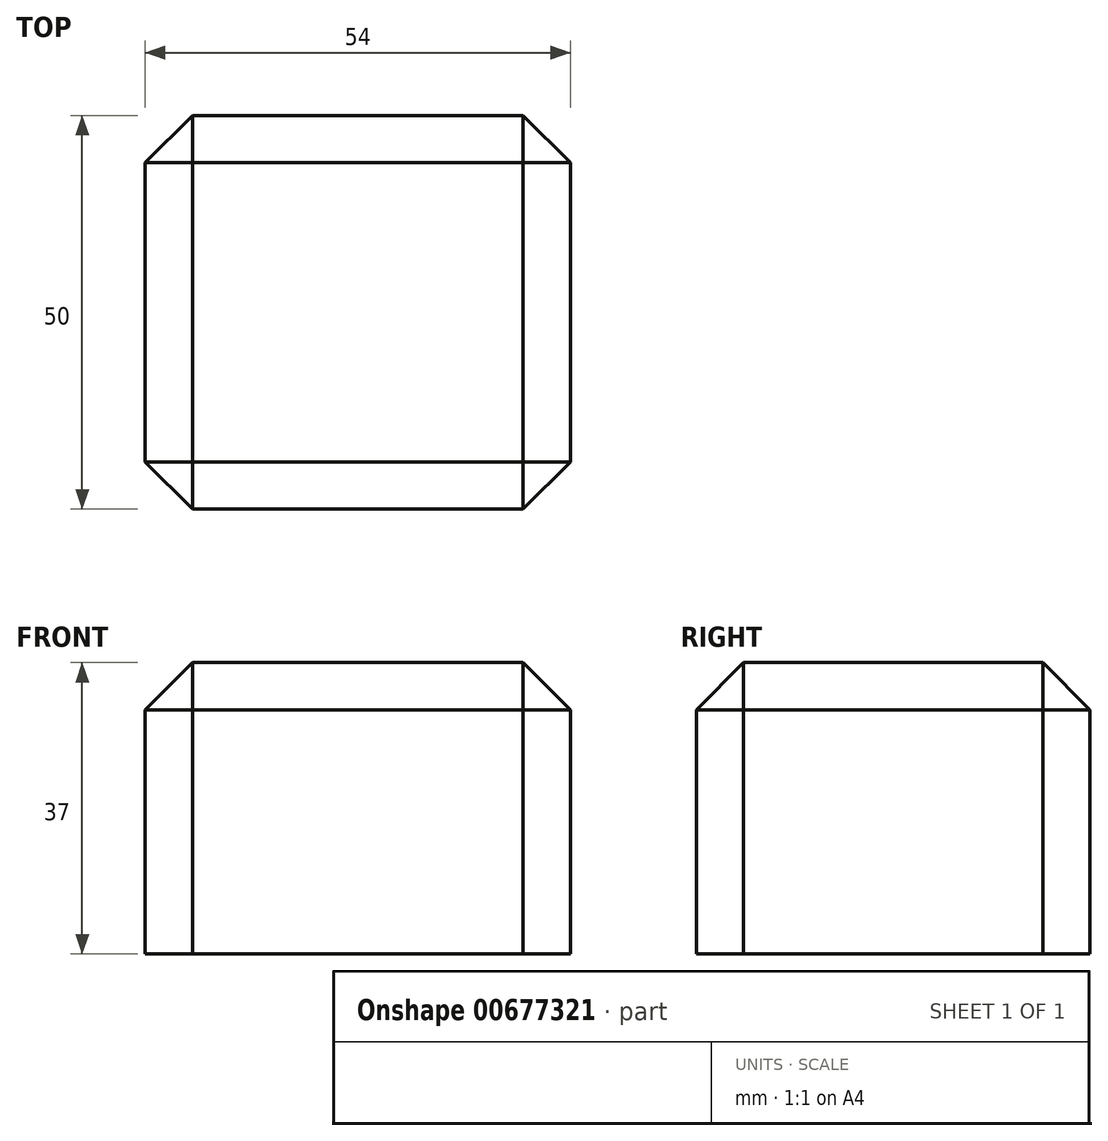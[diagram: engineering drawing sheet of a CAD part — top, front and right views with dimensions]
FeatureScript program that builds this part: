
annotation { "Feature Type Name" : "Feature", "Feature Type Description" : "" }
export const myFeature = defineFeature(function(context is Context, id is Id, definition is map)
    precondition{}
    {
        {
            var Q0;
            Q0=qCreatedBy(makeId("Top.planeOp"),FACE);
            var sketch = newSketch(context, id + "F0", { "sketchPlane" : qUnion([Q0])});
            skLineSegment(sketch, "E0.bottom", {"start": v(27, 25) * mm, "end": v(-27, 25) * mm});
            skLineSegment(sketch, "E0.top", {"start": v(27, -25) * mm, "end": v(-27, -25) * mm});
            skLineSegment(sketch, "E0.left", {"start": v(27, 25) * mm, "end": v(27, -25) * mm});
            skLineSegment(sketch, "E0.right", {"start": v(-27, 25) * mm, "end": v(-27, -25) * mm});
            skPoint(sketch, "E0.middle", {"position": v(0, 0) * mm});
            skSolve(sketch);
        }
        {
            var Q0;
            Q0=makeQuery(id+"F0.imprint","IMPRINT",FACE,{"disambiguationData":[TD([[makeQuery(id+"F0.imprint","IMPRINT",EDGE,{"derivedFrom":sQuery(id+"F0.wireOp",EDGE,"E0.bottom")}),1.0]])]});
            extrude(context, id + "F1", {"entities" : qUnion([Q0]), "depth" : 37 * mm, "offsetDistance" : 25 * mm});
        }
        {
            var Q0;
            Q0=makeQuery(id+"F1.opExtrude","CAP_EDGE",EDGE,{"disambiguationData":[OSD([sQuery(id+"F0.wireOp",EDGE,"E0.top")])],"isStart":false});
            var Q1;
            Q1=makeQuery(id+"F1.opExtrude","CAP_EDGE",EDGE,{"disambiguationData":[OSD([sQuery(id+"F0.wireOp",EDGE,"E0.left")])],"isStart":false});
            var Q2;
            Q2=makeQuery(id+"F1.opExtrude","CAP_EDGE",EDGE,{"disambiguationData":[OSD([sQuery(id+"F0.wireOp",EDGE,"E0.bottom")])],"isStart":false});
            var Q3;
            Q3=makeQuery(id+"F1.opExtrude","CAP_EDGE",EDGE,{"disambiguationData":[OSD([sQuery(id+"F0.wireOp",EDGE,"E0.right")])],"isStart":false});
            var Q4;
            Q4=makeQuery(id+"F1.opExtrude","SWEPT_EDGE",EDGE,{"disambiguationData":[OSD([sQuery(id+"F0.wireOp",EDGE,"E0.top"),sQuery(id+"F0.wireOp",EDGE,"E0.left")])]});
            var Q5;
            Q5=makeQuery(id+"F1.opExtrude","SWEPT_EDGE",EDGE,{"disambiguationData":[OSD([sQuery(id+"F0.wireOp",EDGE,"E0.bottom"),sQuery(id+"F0.wireOp",EDGE,"E0.left")])]});
            var Q6;
            Q6=makeQuery(id+"F1.opExtrude","SWEPT_EDGE",EDGE,{"disambiguationData":[OSD([sQuery(id+"F0.wireOp",EDGE,"E0.top"),sQuery(id+"F0.wireOp",EDGE,"E0.right")])]});
            var Q7;
            Q7=makeQuery(id+"F1.opExtrude","SWEPT_EDGE",EDGE,{"disambiguationData":[OSD([sQuery(id+"F0.wireOp",EDGE,"E0.bottom"),sQuery(id+"F0.wireOp",EDGE,"E0.right")])]});
            chamfer(context, id + "F2", {"entities" : qUnion([Q0, Q1, Q2, Q3, Q4, Q5, Q6, Q7]), "width" : 6 * mm, "tangentPropagation" : true});
        }
    });
